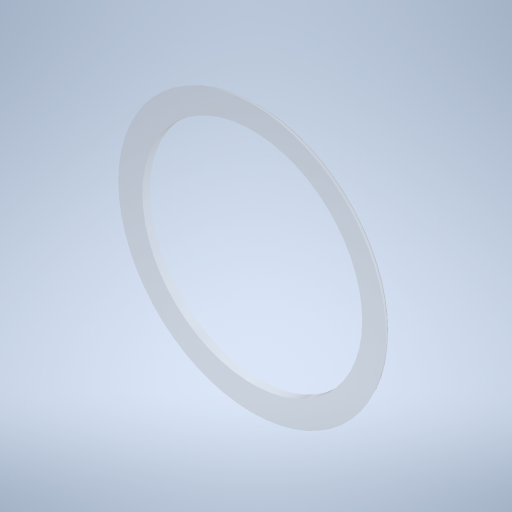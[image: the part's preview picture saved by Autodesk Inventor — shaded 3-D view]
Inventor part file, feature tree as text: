
AUTODESK INVENTOR PART (.ipt)
format: ipt  version: 2023 (Build 270158000, 158)  size: 273,920 bytes
history: native  units: mm
features: reference x4, other x3, extrude x1, fillet x1, sketch x1
ambient origin geometry x8: Origin, YZ Plane, XZ Plane, XY Plane, X Axis, Y Axis, Z Axis, Center Point
bodies: Solido1 (feature_tree)
feature tree (10):
  extrude  "Estrusione1"  Depth=1.5mm TaperAngle=0.0deg
  fillet  "Raccordo1"  Radius=2.0mm
  sketch  "Schizzo1"
  reference  "Riferimento1"
  reference  "Riferimento2"
  reference  "Riferimento3"
  reference  "Riferimento4"
  other  "08-20-2023-assieme con riduttore.iam"
  other  "Sony_E-Mount_Body_Cap:1"
  other  "CE2_adaptor_thin_2_v7:1"
